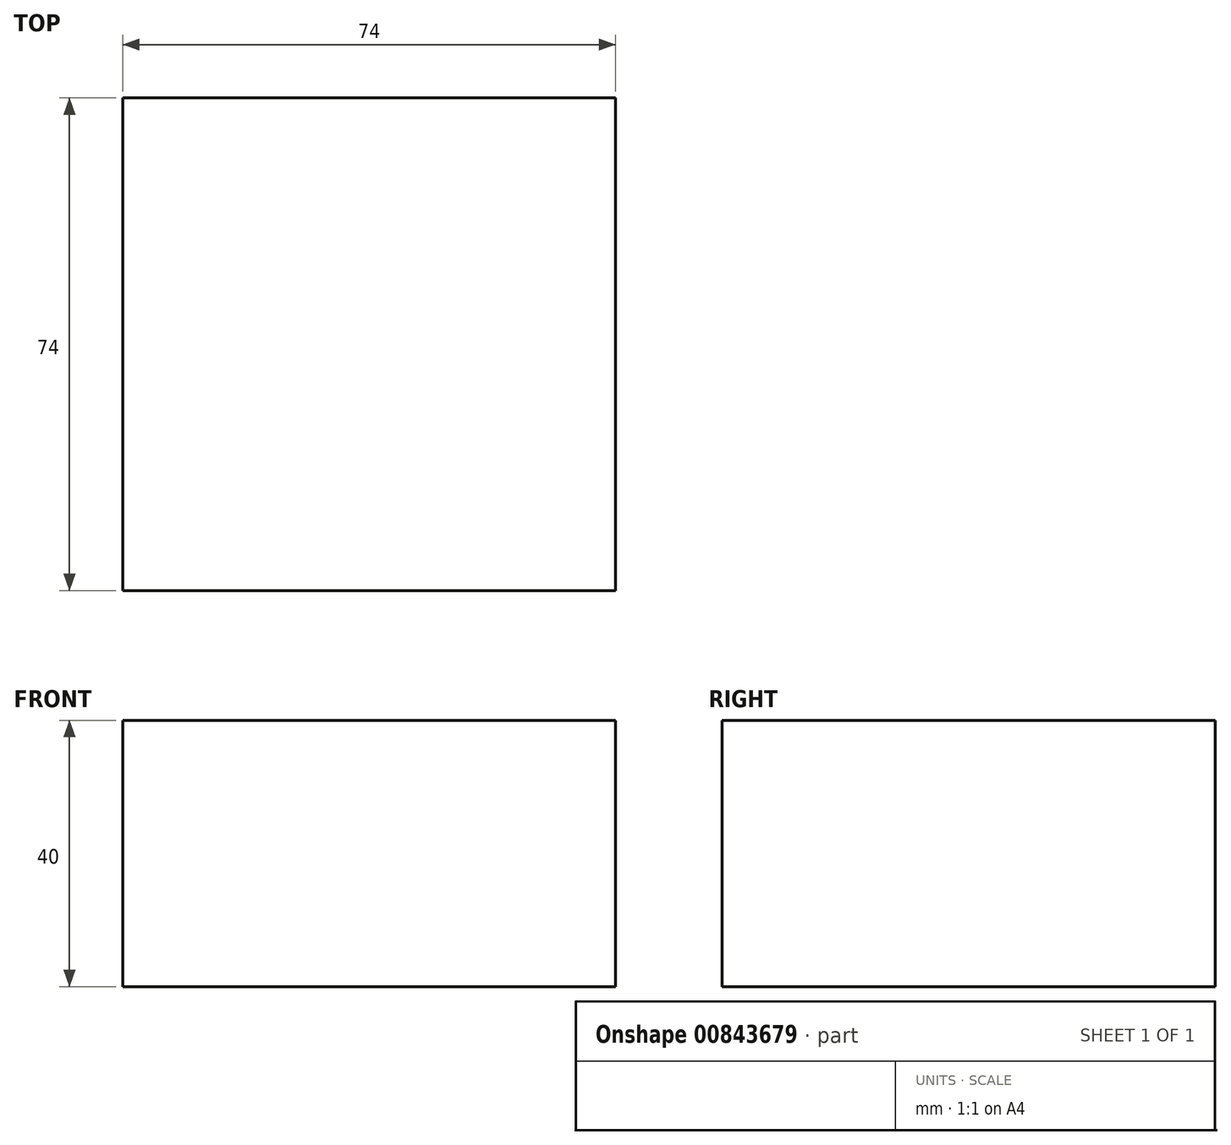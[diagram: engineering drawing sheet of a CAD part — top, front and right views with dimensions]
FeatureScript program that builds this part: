
annotation { "Feature Type Name" : "Feature", "Feature Type Description" : "" }
export const myFeature = defineFeature(function(context is Context, id is Id, definition is map)
    precondition{}
    {
        {
            var Q0;
            Q0=qCreatedBy(makeId("Top.planeOp"),FACE);
            var sketch = newSketch(context, id + "F0", { "sketchPlane" : qUnion([Q0])});
            skLineSegment(sketch, "E0.bottom", {"start": v(37, -37) * mm, "end": v(-37, -37) * mm});
            skLineSegment(sketch, "E0.top", {"start": v(37, 37) * mm, "end": v(-37, 37) * mm});
            skLineSegment(sketch, "E0.left", {"start": v(37, -37) * mm, "end": v(37, 37) * mm});
            skLineSegment(sketch, "E0.right", {"start": v(-37, -37) * mm, "end": v(-37, 37) * mm});
            skPoint(sketch, "E0.middle", {"position": v(0, 0) * mm});
            skSolve(sketch);
        }
        {
            var Q0;
            Q0=makeQuery(id+"F0.imprint","IMPRINT",FACE,{"disambiguationData":[TD([[makeQuery(id+"F0.imprint","IMPRINT",EDGE,{"derivedFrom":sQuery(id+"F0.wireOp",EDGE,"E0.bottom")}),-1.0]])]});
            extrude(context, id + "F1", {"entities" : qUnion([Q0]), "depth" : 40 * mm, "offsetDistance" : 25 * mm});
        }
    });
